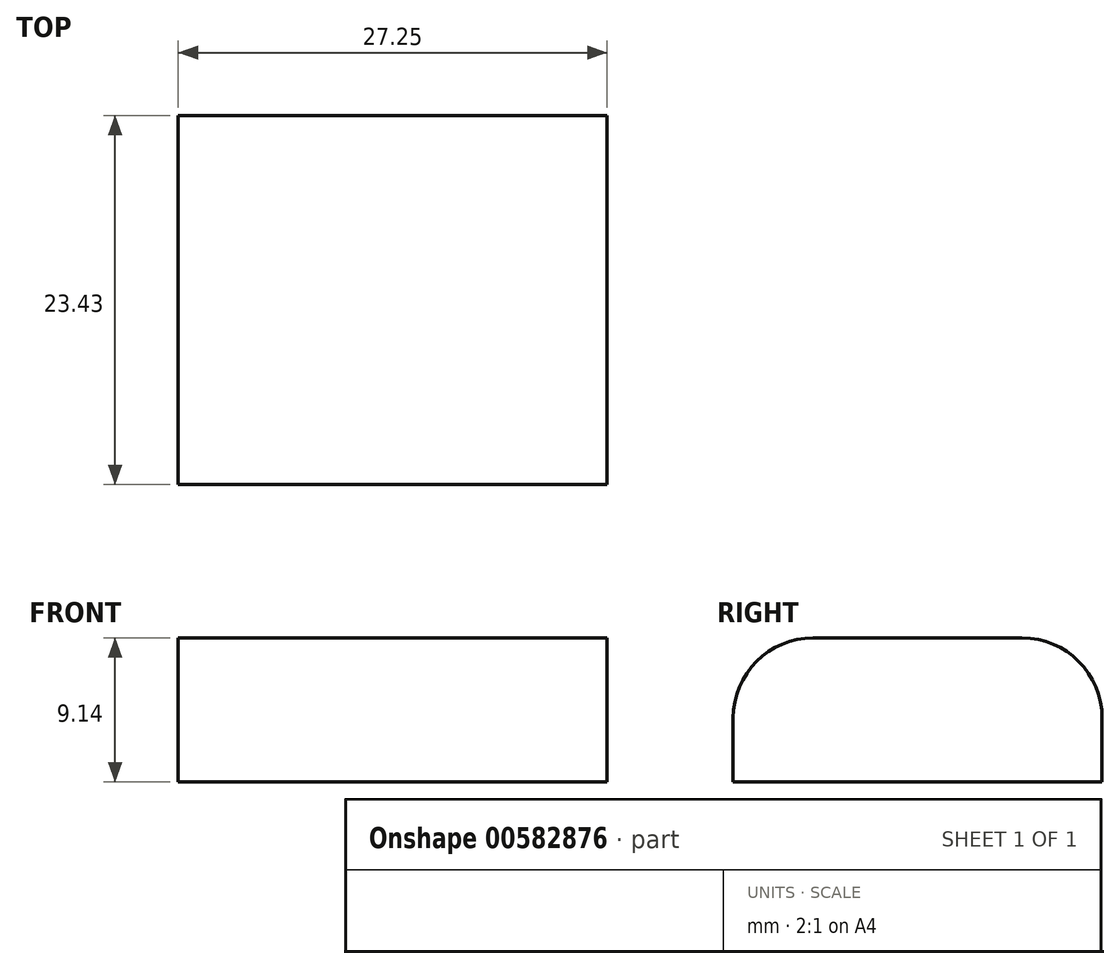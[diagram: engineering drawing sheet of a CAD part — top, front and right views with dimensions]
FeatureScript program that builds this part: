
annotation { "Feature Type Name" : "Feature", "Feature Type Description" : "" }
export const myFeature = defineFeature(function(context is Context, id is Id, definition is map)
    precondition{}
    {
        {
            var Q0;
            Q0=qCreatedBy(makeId("Top.planeOp"),FACE);
            var sketch = newSketch(context, id + "F0", { "sketchPlane" : qUnion([Q0])});
            skLineSegment(sketch, "E0.bottom", {"start": v(0, 0) * mm, "end": v(-27.25, 0) * mm});
            skLineSegment(sketch, "E0.top", {"start": v(0, -23.43) * mm, "end": v(-27.25, -23.43) * mm});
            skLineSegment(sketch, "E0.left", {"start": v(0, 0) * mm, "end": v(0, -23.43) * mm});
            skLineSegment(sketch, "E0.right", {"start": v(-27.25, 0) * mm, "end": v(-27.25, -23.43) * mm});
            skSolve(sketch);
        }
        {
            var Q0;
            Q0 = qSketchRegion(id + "F0", true);
            extrude(context, id + "F1", {"entities" : qUnion([Q0]), "depth" : 9.14 * mm, "offsetDistance" : 25.4 * mm});
        }
        {
            var Q0;
            Q0=makeQuery(id+"F1.opExtrude","CAP_EDGE",EDGE,{"disambiguationData":[OSD([sQuery(id+"F0.wireOp",EDGE,"E0.bottom")])],"isStart":false});
            var Q1;
            Q1=makeQuery(id+"F1.opExtrude","CAP_EDGE",EDGE,{"disambiguationData":[OSD([sQuery(id+"F0.wireOp",EDGE,"E0.top")])],"isStart":false});
            fillet(context, id + "F2", {"entities" : qUnion([Q0, Q1]), "radius" : 5.08 * mm, "tangentPropagation" : true, "allowEdgeOverflow" : false});
        }
    });
